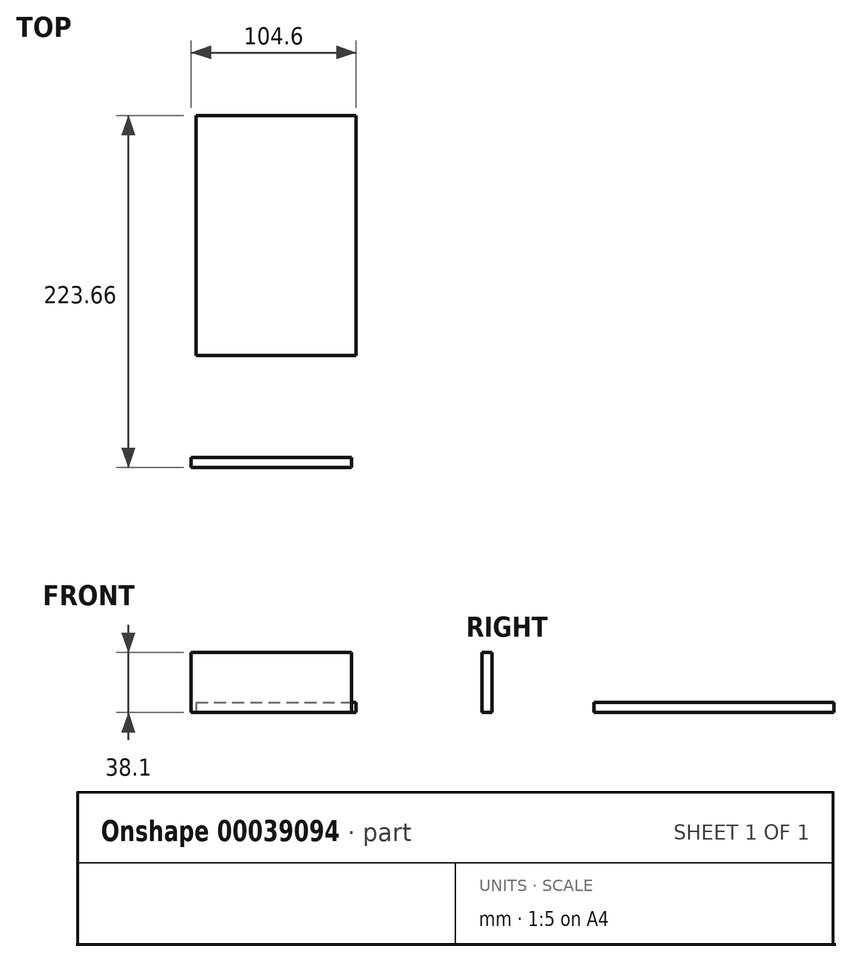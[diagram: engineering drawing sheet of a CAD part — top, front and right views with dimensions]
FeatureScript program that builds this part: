
annotation { "Feature Type Name" : "Feature", "Feature Type Description" : "" }
export const myFeature = defineFeature(function(context is Context, id is Id, definition is map)
    precondition{}
    {
        {
            var Q0;
            Q0=qCreatedBy(makeId("Top.planeOp"),FACE);
            var sketch = newSketch(context, id + "F0", { "sketchPlane" : qUnion([Q0])});
            skLineSegment(sketch, "E0.bottom", {"start": v(-141.87, 116.39) * mm, "end": v(-40.27, 116.39) * mm});
            skLineSegment(sketch, "E0.top", {"start": v(-141.87, -36.01) * mm, "end": v(-40.27, -36.01) * mm});
            skLineSegment(sketch, "E0.left", {"start": v(-141.87, 116.39) * mm, "end": v(-141.87, -36.01) * mm});
            skLineSegment(sketch, "E0.right", {"start": v(-40.27, 116.39) * mm, "end": v(-40.27, -36.01) * mm});
            skSolve(sketch);
        }
        {
            var Q0;
            Q0=makeQuery(id+"F0.imprint","IMPRINT",FACE,{"disambiguationData":[TD([[makeQuery(id+"F0.imprint","IMPRINT",EDGE,{"derivedFrom":sQuery(id+"F0.wireOp",EDGE,"E0.bottom")}),-1.0]])]});
            extrude(context, id + "F1", {"entities" : qUnion([Q0]), "depth" : 6.35 * mm});
        }
        {
            var Q0;
            Q0=qCreatedBy(makeId("Top.planeOp"),FACE);
            var sketch = newSketch(context, id + "F2", { "sketchPlane" : qUnion([Q0])});
            skLineSegment(sketch, "E1.bottom", {"start": v(-144.87, -100.92) * mm, "end": v(-43.27, -100.92) * mm});
            skLineSegment(sketch, "E1.top", {"start": v(-144.87, -107.27) * mm, "end": v(-43.27, -107.27) * mm});
            skLineSegment(sketch, "E1.left", {"start": v(-144.87, -100.92) * mm, "end": v(-144.87, -107.27) * mm});
            skLineSegment(sketch, "E1.right", {"start": v(-43.27, -100.92) * mm, "end": v(-43.27, -107.27) * mm});
            skSolve(sketch);
        }
        {
            var Q0;
            Q0=makeQuery(id+"F2.imprint","IMPRINT",FACE,{"disambiguationData":[TD([[makeQuery(id+"F2.imprint","IMPRINT",EDGE,{"derivedFrom":sQuery(id+"F2.wireOp",EDGE,"E1.bottom")}),-1.0]])]});
            extrude(context, id + "F3", {"entities" : qUnion([Q0]), "depth" : 38.1 * mm});
        }
    });
